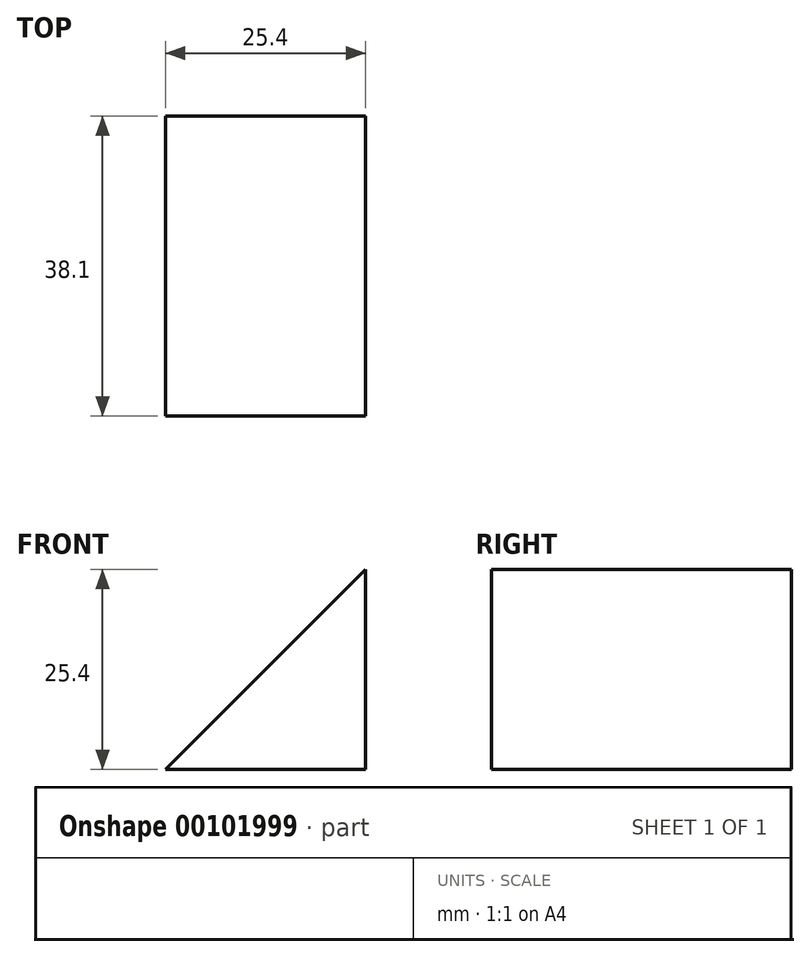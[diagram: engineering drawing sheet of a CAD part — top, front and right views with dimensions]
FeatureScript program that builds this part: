
annotation { "Feature Type Name" : "Feature", "Feature Type Description" : "" }
export const myFeature = defineFeature(function(context is Context, id is Id, definition is map)
    precondition{}
    {
        {
            var Q0;
            Q0=qCreatedBy(makeId("Front.planeOp"),FACE);
            var sketch = newSketch(context, id + "F0", { "sketchPlane" : qUnion([Q0])});
            skLineSegment(sketch, "E0", {"start": v(0, 0) * mm, "end": v(25.4, 25.4) * mm});
            skLineSegment(sketch, "E1", {"start": v(25.4, 25.4) * mm, "end": v(25.4, 0) * mm});
            skLineSegment(sketch, "E2", {"start": v(25.4, 0) * mm, "end": v(0, 0) * mm});
            skLineSegment(sketch, "E3", {"start": v(12.7, 12.7) * mm, "end": v(12.7, 0) * mm});
            skSolve(sketch);
        }
        {
            var Q0;
            Q0 = qSketchRegion(id + "F0", true);
            extrude(context, id + "F1", {"entities" : qUnion([Q0]), "depth" : 38.1 * mm});
        }
    });
